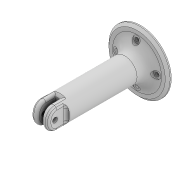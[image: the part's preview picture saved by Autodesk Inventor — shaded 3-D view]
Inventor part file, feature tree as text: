
AUTODESK INVENTOR PART (.ipt)
format: ipt  version: 2022 (Build 260153000, 153)  size: 325,120 bytes
history: native  units: mm
features: extrude x7, sketch x7, fillet x3, projected_geometry x3, other x1, chamfer x1
ambient origin geometry x8: Origin, YZ Plane, XZ Plane, XY Plane, X Axis, Y Axis, Z Axis, Center Point
bodies: Body1 (feature_tree)
feature tree (22):
  other  "Sólido1"
  extrude  "Extrusión1"  Depth=3.0mm TaperAngle=0.0deg
  extrude  "Extrusión2"  Depth=80.0mm TaperAngle=0.0deg
  extrude  "Extrusión3"  Depth=2.0mm
  extrude  "Extrusión4"  Depth=5.0mm
  fillet  "Empalme1"  Radius=15.0mm
  fillet  "Empalme2"  [1 undecoded]
  fillet  "Empalme3"  Radius=7.5mm
  extrude  "Extrusión9"  Depth=6.0mm
  extrude  "Extrusión10"  Depth=10.0mm
  extrude  "Extrusión11"  Depth=2.0mm TaperAngle=0.0deg
  chamfer  "Chaflán1"  Distance=3.2mm
  sketch  "Boceto1"  dims[d0=50.0mm d1=3.0mm d2=0.0mm]
  sketch  "Boceto2"  dims[d3=20.0mm d4=80.0mm d5=0.0mm]
  sketch  "Boceto3"  dims[d6=4.0mm d7=2.0mm]
  projected_geometry  "Contorno proyectado1"
  sketch  "Boceto4"  dims[d8=5.0mm d9=5.0mm d10=15.0mm d11=0.0mm d13=0.0mm d14=0.0mm d15=7.5mm]
  projected_geometry  "Contorno proyectado2"
  sketch  "Boceto9"  dims[d16=4.0mm d17=6.0mm]
  sketch  "Boceto10"  dims[d18=2.0mm d39=10.0mm]
  projected_geometry  "Contorno proyectado7"
  sketch  "Boceto11"  dims[d40=16.0mm d41=64.0mm d42=0.0mm d43=3.2mm d44=3.2mm d45=3.2mm d46=3.2mm d47=0.0mm d48=0.0mm d49=6.0mm d50=6.0mm d51=6.0mm d52=6.0mm d53=0.0mm d54=0.0mm d55=2.0mm d56=2.0mm d57=45.0deg]
note: 1 required parameter value undecoded (feature->parameter linkage not recoverable at this tier; creation-order binding heuristic only, values carry confidence <= 0.55)
